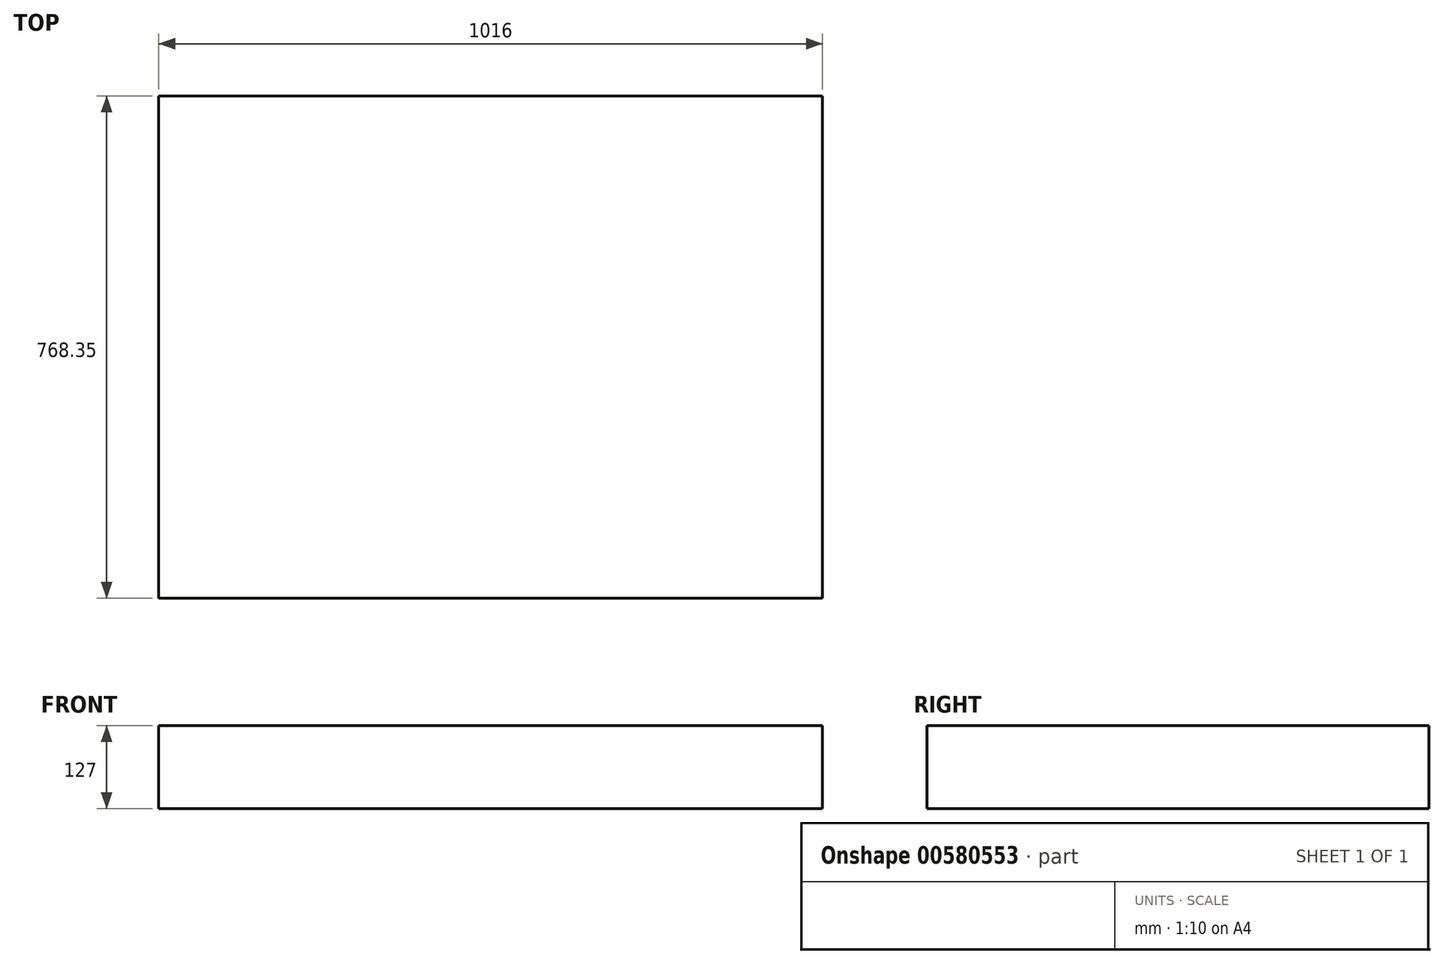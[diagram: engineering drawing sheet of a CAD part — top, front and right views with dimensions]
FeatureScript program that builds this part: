
annotation { "Feature Type Name" : "Feature", "Feature Type Description" : "" }
export const myFeature = defineFeature(function(context is Context, id is Id, definition is map)
    precondition{}
    {
        {
            var Q0;
            Q0=qCreatedBy(makeId("Top.planeOp"),FACE);
            var sketch = newSketch(context, id + "F0", { "sketchPlane" : qUnion([Q0])});
            skLineSegment(sketch, "E0.bottom", {"start": v(-550.51, -375.38) * mm, "end": v(465.49, -375.38) * mm});
            skLineSegment(sketch, "E0.top", {"start": v(-550.51, 392.97) * mm, "end": v(465.49, 392.97) * mm});
            skLineSegment(sketch, "E0.left", {"start": v(-550.51, -375.38) * mm, "end": v(-550.51, 392.97) * mm});
            skLineSegment(sketch, "E0.right", {"start": v(465.49, -375.38) * mm, "end": v(465.49, 392.97) * mm});
            skSolve(sketch);
        }
        {
            var Q0;
            Q0 = qSketchRegion(id + "F0", true);
            extrude(context, id + "F1", {"entities" : qUnion([Q0]), "depth" : 127 * mm, "offsetDistance" : 25.4 * mm});
        }
    });
